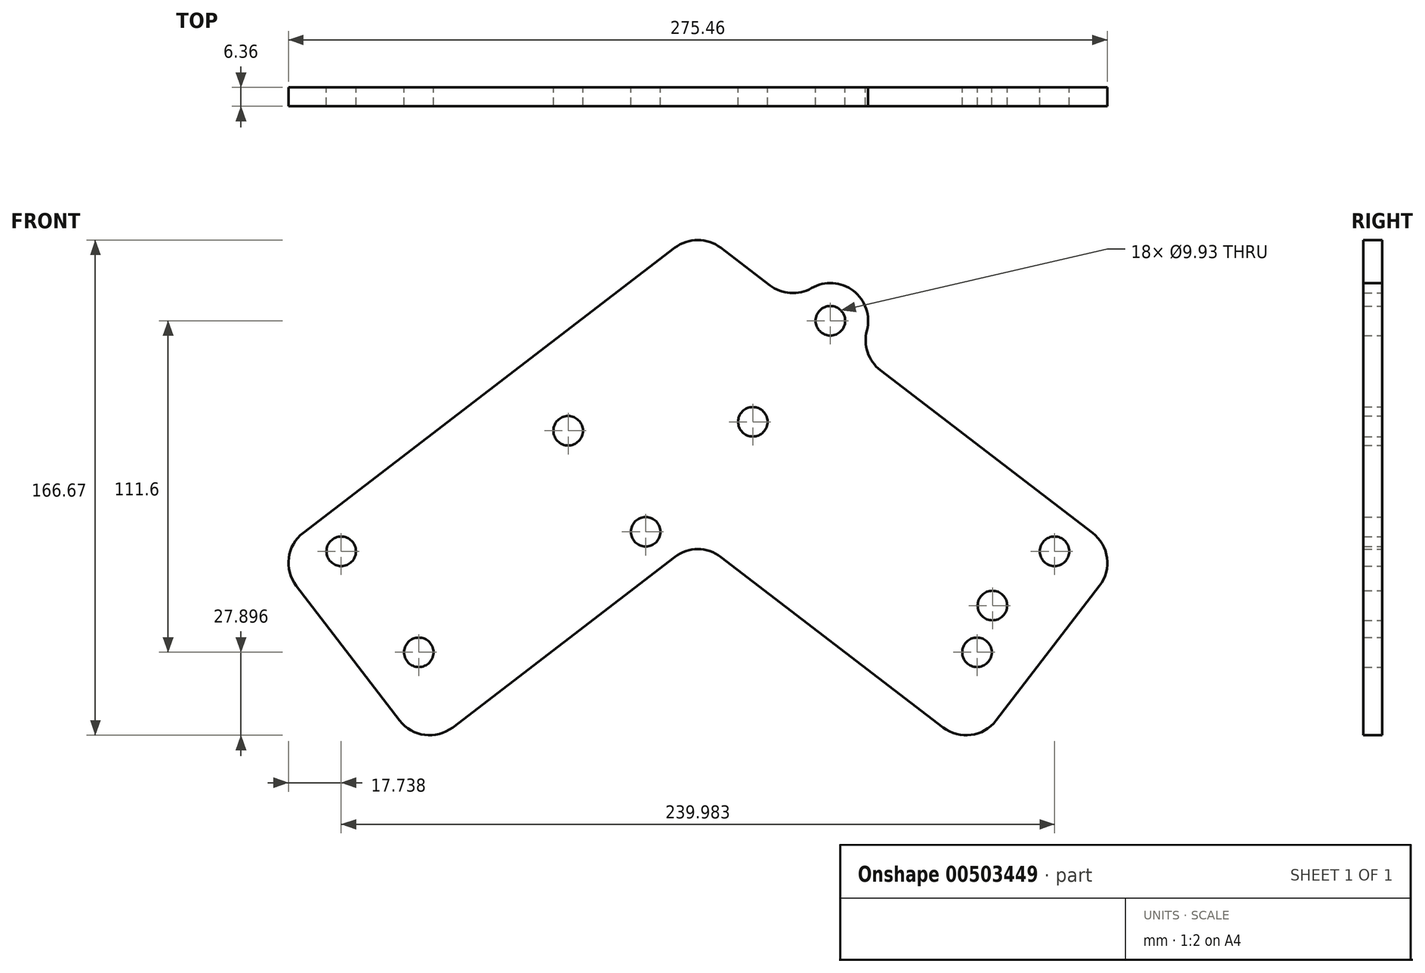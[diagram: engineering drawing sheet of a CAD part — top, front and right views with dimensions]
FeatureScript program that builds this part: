
annotation { "Feature Type Name" : "Feature", "Feature Type Description" : "" }
export const myFeature = defineFeature(function(context is Context, id is Id, definition is map)
    precondition{}
    {
        {
            var Q0;
            Q0=qCreatedBy(makeId("Front.planeOp"),FACE);
            var sketch = newSketch(context, id + "F0", { "sketchPlane" : qUnion([Q0])});
            skLineSegment(sketch, "E0", {"start": v(0, 0) * mm, "end": v(-92.58, -71.04) * mm});
            skLineSegment(sketch, "E1", {"start": v(0, 0) * mm, "end": v(0, 104.05) * mm});
            skLineSegment(sketch, "E2", {"start": v(-92.58, -71.04) * mm, "end": v(-142.84, -5.55) * mm});
            skLineSegment(sketch, "E3", {"start": v(-142.84, -5.55) * mm, "end": v(0, 104.05) * mm});
            skPoint(sketch, "E4", {"position": v(-15.88, 109.88) * mm});
            skPoint(sketch, "E5", {"position": v(-15.88, -30.2) * mm});
            skLineSegment(sketch, "E6.MirrorCS", {"start": v(0, 0) * mm, "end": v(92.58, -71.04) * mm});
            skPoint(sketch, "E7.MirrorP", {"position": v(15.88, -30.2) * mm});
            skLineSegment(sketch, "E8.MirrorCS", {"start": v(92.58, -71.04) * mm, "end": v(142.84, -5.55) * mm});
            skLineSegment(sketch, "E9.MirrorCS", {"start": v(142.84, -5.55) * mm, "end": v(0, 104.05) * mm});
            skPoint(sketch, "E10.MirrorP", {"position": v(15.88, 109.88) * mm});
            skLineSegment(sketch, "E11", {"start": v(-15.88, -30.2) * mm, "end": v(-62.26, 30.26) * mm, "construction": true});
            skLineSegment(sketch, "E12", {"start": v(-15.88, 109.88) * mm, "end": v(30.51, 49.43) * mm, "construction": true});
            skCircle(sketch, "E13", {"center": v(-93.9, -38.03) * mm, "radius": 4.97 * mm});
            skLineSegment(sketch, "E14", {"start": v(-93.9, -38.03) * mm, "end": v(-127.72, 6.05) * mm, "construction": true});
            skCircle(sketch, "E15", {"center": v(-120, -4.03) * mm, "radius": 4.97 * mm});
            skCircle(sketch, "E16.MirrorC", {"center": v(93.9, -38.03) * mm, "radius": 4.97 * mm});
            skCircle(sketch, "E17.MirrorC", {"center": v(120, -4.03) * mm, "radius": 4.97 * mm});
            skCircle(sketch, "E18", {"center": v(-43.65, 36.54) * mm, "radius": 4.97 * mm});
            skLineSegment(sketch, "E19", {"start": v(-43.65, 36.54) * mm, "end": v(-9.82, -7.54) * mm});
            skCircle(sketch, "E20", {"center": v(-17.55, 2.54) * mm, "radius": 4.97 * mm});
            skPoint(sketch, "E21", {"position": v(-110.81, -16) * mm});
            skCircle(sketch, "E22", {"center": v(44.58, 73.57) * mm, "radius": 4.97 * mm});
            skCircle(sketch, "E23", {"center": v(18.48, 39.56) * mm, "radius": 4.97 * mm});
            skArc(sketch, "E24", {"start": v(52.58, 63.7) * mm, "mid": v(52.3, 83.64) * mm, "end": v(32.98, 78.74) * mm});
            skPoint(sketch, "E25", {"position": v(52.58, 63.7) * mm});
            skPoint(sketch, "E26", {"position": v(32.98, 78.74) * mm});
            skCircle(sketch, "E27", {"center": v(99.09, -22.29) * mm, "radius": 4.97 * mm});
            skSolve(sketch);
        }
        {
            var Q0;
            Q0=qSketchRegion(id+"F0",true);
            extrude(context, id + "F1", {"entities" : qUnion([Q0]), "depth" : 6.35 * mm, "offsetDistance" : 25.4 * mm, "symmetric" : true});
        }
        {
            var Q0;
            Q0=makeQuery(id+"F1.opExtrude","SWEPT_EDGE",EDGE,{"disambiguationData":[OSD([sQuery(id+"F0.wireOp",EDGE,"E2"),sQuery(id+"F0.wireOp",EDGE,"E3")])]});
            var Q1;
            Q1=makeQuery(id+"F1.opExtrude","SWEPT_EDGE",EDGE,{"disambiguationData":[OSD([sQuery(id+"F0.wireOp",EDGE,"E3"),sQuery(id+"F0.wireOp",EDGE,"E1"),sQuery(id+"F0.wireOp",EDGE,"E9.MirrorCS")])]});
            var Q2;
            Q2=makeQuery(id+"F1.opExtrude","SWEPT_EDGE",EDGE,{"disambiguationData":[OSD([sQuery(id+"F0.wireOp",EDGE,"E0"),sQuery(id+"F0.wireOp",EDGE,"E6.MirrorCS"),sQuery(id+"F0.wireOp",EDGE,"E1")])]});
            var Q3;
            Q3=makeQuery(id+"F1.opExtrude","SWEPT_EDGE",EDGE,{"disambiguationData":[OSD([sQuery(id+"F0.wireOp",EDGE,"E6.MirrorCS"),sQuery(id+"F0.wireOp",EDGE,"E8.MirrorCS")])]});
            var Q4;
            Q4=makeQuery(id+"F1.opExtrude","SWEPT_EDGE",EDGE,{"disambiguationData":[OSD([sQuery(id+"F0.wireOp",EDGE,"E8.MirrorCS"),sQuery(id+"F0.wireOp",EDGE,"E9.MirrorCS")])]});
            var Q5;
            Q5=makeQuery(id+"F1.opExtrude","SWEPT_EDGE",EDGE,{"disambiguationData":[OSD([sQuery(id+"F0.wireOp",EDGE,"E0"),sQuery(id+"F0.wireOp",EDGE,"E2")])]});
            var Q6;
            {var subQ0=sQuery(id+"F0.wireOp",EDGE,"E24");var subQ1=sQuery(id+"F0.wireOp",EDGE,"E9.MirrorCS");Q6=makeQuery(id+"F1.opExtrude","SWEPT_EDGE",EDGE,{"disambiguationData":[OSD([subQ1,subQ0]),TDD([makeQuery(id+"F0.imprint","INTERSECT",VERTEX,{"disambiguationData":[OD(1.0)],"derivedFrom":[subQ1,subQ0]})])]});}
            var Q7;
            {var subQ0=sQuery(id+"F0.wireOp",EDGE,"E24");var subQ1=sQuery(id+"F0.wireOp",EDGE,"E9.MirrorCS");Q7=makeQuery(id+"F1.opExtrude","SWEPT_EDGE",EDGE,{"disambiguationData":[OSD([subQ1,subQ0]),TDD([makeQuery(id+"F0.imprint","INTERSECT",VERTEX,{"disambiguationData":[OD(0.0)],"derivedFrom":[subQ1,subQ0]})])]});}
            fillet(context, id + "F2", {"entities" : qUnion([Q0, Q1, Q2, Q3, Q4, Q5, Q6, Q7]), "radius" : 12.7 * mm, "tangentPropagation" : true, "allowEdgeOverflow" : false});
        }
    });
